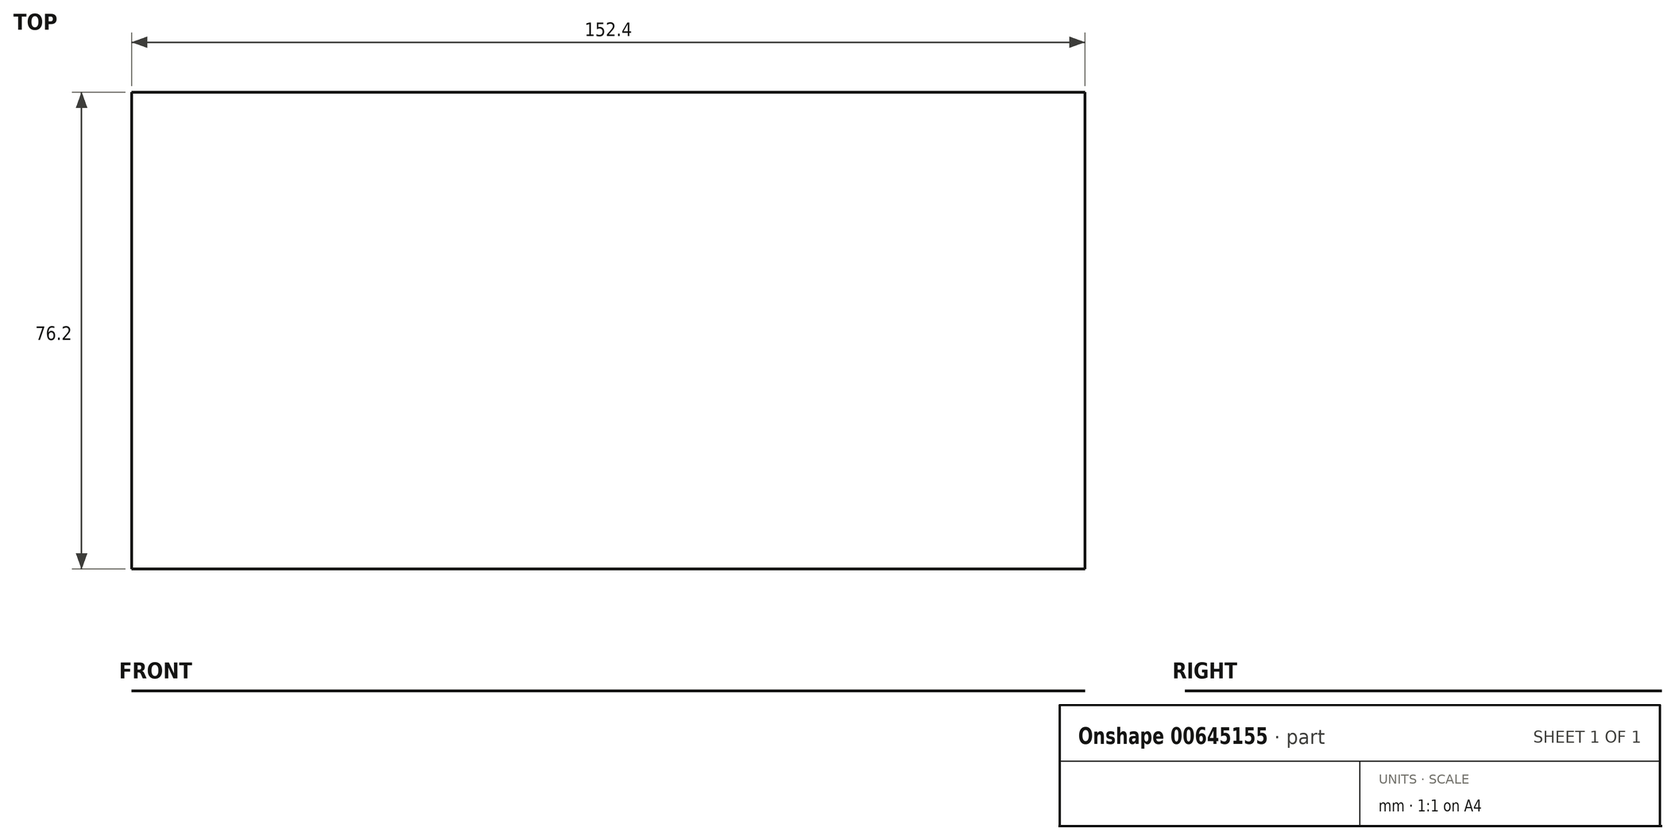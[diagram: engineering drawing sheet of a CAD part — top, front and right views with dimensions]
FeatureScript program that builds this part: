
annotation { "Feature Type Name" : "Feature", "Feature Type Description" : "" }
export const myFeature = defineFeature(function(context is Context, id is Id, definition is map)
    precondition{}
    {
        {
            var Q0;
            Q0=qCreatedBy(makeId("Top.planeOp"),FACE);
            var sketch = newSketch(context, id + "F0", { "sketchPlane" : qUnion([Q0])});
            skLineSegment(sketch, "E0.bottom", {"start": v(76.2, 38.1) * mm, "end": v(-76.2, 38.1) * mm});
            skLineSegment(sketch, "E0.top", {"start": v(76.2, -38.1) * mm, "end": v(-76.2, -38.1) * mm});
            skLineSegment(sketch, "E0.left", {"start": v(76.2, 38.1) * mm, "end": v(76.2, -38.1) * mm});
            skLineSegment(sketch, "E0.right", {"start": v(-76.2, 38.1) * mm, "end": v(-76.2, -38.1) * mm});
            skPoint(sketch, "E0.middle", {"position": v(0, 0) * mm});
            skSolve(sketch);
        }
        {
            var Q0;
            Q0=makeQuery(id+"F0.imprint","IMPRINT",FACE,{"disambiguationData":[TD([[makeQuery(id+"F0.imprint","IMPRINT",EDGE,{"derivedFrom":sQuery(id+"F0.wireOp",EDGE,"E0.bottom")}),1.0]])]});
            extrude(context, id + "F1", {"entities" : qUnion([Q0]), "depth" : 1 / 406.4 * mm, "offsetDistance" : 25.4 * mm});
        }
    });
